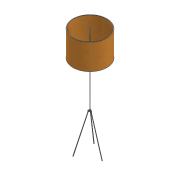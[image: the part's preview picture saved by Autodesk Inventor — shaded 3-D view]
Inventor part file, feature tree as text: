
AUTODESK INVENTOR PART (.ipt)
format: ipt  version: 2020.2 (Build 242310000, 310)  size: 216,064 bytes
history: native  units: mm
features: sketch x9, extrude x5, plane x5, loft x3, shell x1, delete_face x1
ambient origin geometry x8: Origin, YZ Plane, XZ Plane, XY Plane, X Axis, Y Axis, Z Axis, Center Point
bodies: Solid1 (feature_tree), Solid2 (feature_tree)
feature tree (24):
  extrude  "Extrusion1"  Depth=1000.0mm TaperAngle=0.0deg
  plane  "Work Plane1"
  extrude  "Extrusion2"  TaperAngle=60.0deg  [1 undecoded]
  plane  "Work Plane2"
  plane  "Work Plane3"
  sketch  "Sketch3"  dims[d6=15.0mm d7=0.0mm d8=0.0mm]
  sketch  "Sketch8"  dims[d9=650.0mm d20=10.0mm]
  sketch  "Sketch9"  dims[d21=10.0mm d22=10.0mm]
  sketch  "Sketch10"  dims[d23=0.0mm d24=90.0deg d25=0.0mm d26=90.0deg]
  loft  "Loft1"
  loft  "Loft2"
  loft  "Loft3"
  plane  "Work Plane4"
  extrude  "Extrusion3"  TaperAngle=0.0deg  [1 undecoded]
  plane  "Work Plane5"
  extrude  "Extrusion4"  TaperAngle=0.0deg  [1 undecoded]
  shell  "Shell1"  Thickness=0.0mm
  delete_face  "Delete Face1"
  extrude  "Extrusion5"  [1 undecoded]
  sketch  "Sketch1"  dims[d0=15.0mm d1=1000.0mm d2=0.0mm]
  sketch  "Sketch2"  dims[d3=0.0mm d5=60.0deg]
  sketch  "Sketch11"  dims[d27=0.0mm d28=90.0deg d29=0.0mm d30=90.0deg d31=0.0mm d32=90.0deg]
  sketch  "Sketch12"  dims[d33=0.0mm d34=90.0deg d35=-350.0mm]
  sketch  "Sketch13"  dims[d36=150.0mm d37=15.0mm d38=0.0mm d39=0.0mm d40=600.0mm d41=250.0mm d42=200.0mm d43=0.0mm d44=0.0mm d45=10.0mm d46=280.0mm d47=0.0mm]
note: 4 required parameter values undecoded (feature->parameter linkage not recoverable at this tier; creation-order binding heuristic only, values carry confidence <= 0.55)
